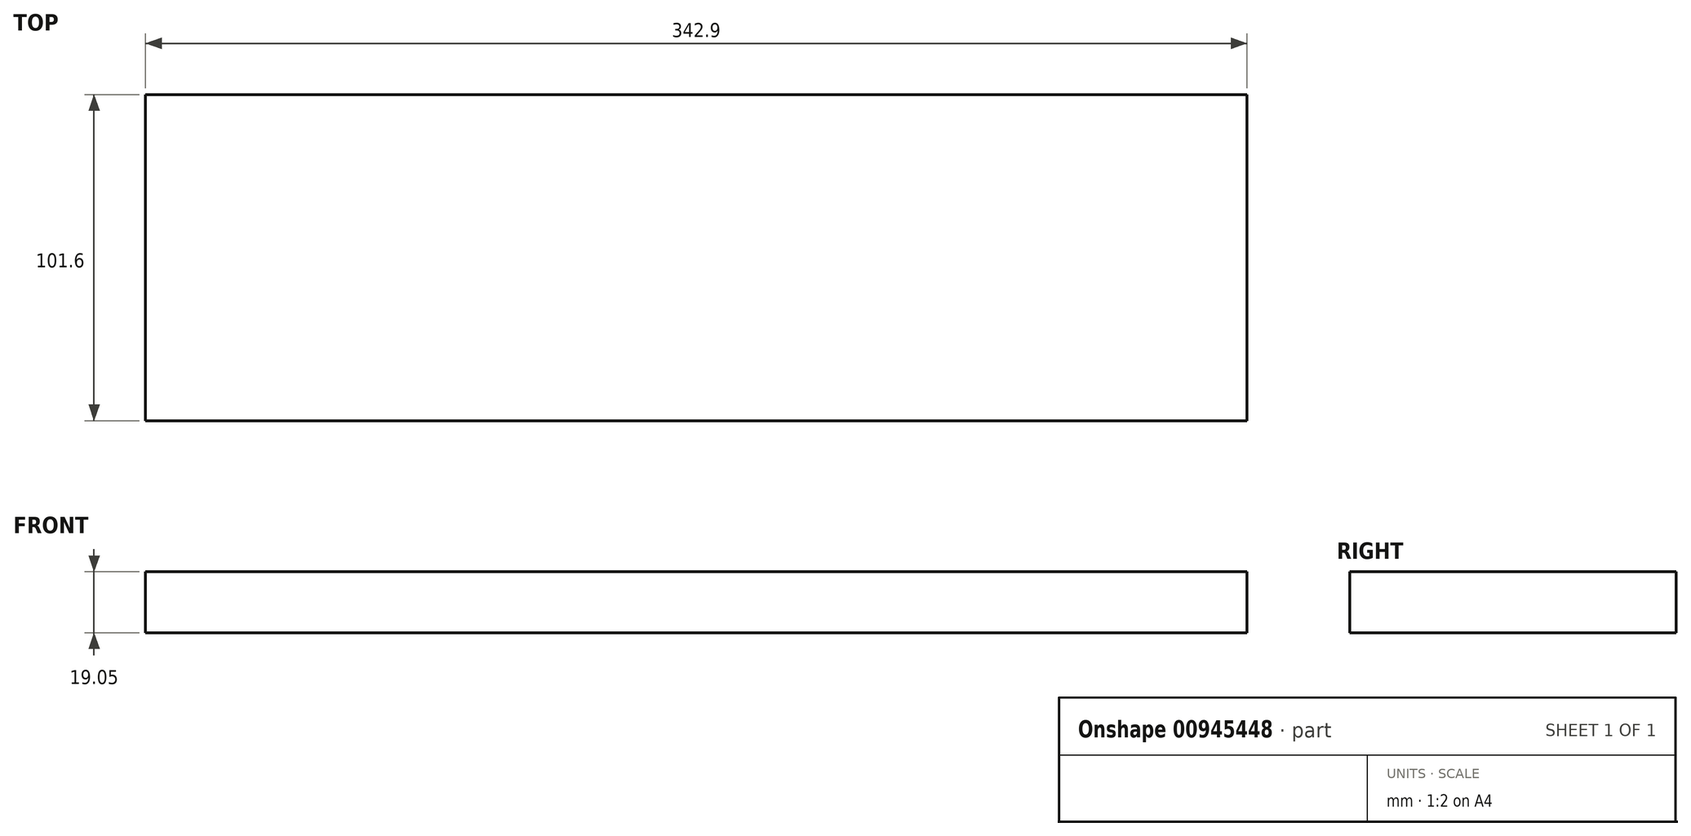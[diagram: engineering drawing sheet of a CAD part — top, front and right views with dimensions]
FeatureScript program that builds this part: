
annotation { "Feature Type Name" : "Feature", "Feature Type Description" : "" }
export const myFeature = defineFeature(function(context is Context, id is Id, definition is map)
    precondition{}
    {
        {
            var Q0;
            Q0=qCreatedBy(makeId("Top.planeOp"),FACE);
            var sketch = newSketch(context, id + "F0", { "sketchPlane" : qUnion([Q0])});
            skLineSegment(sketch, "E0.bottom", {"start": v(0, 0) * mm, "end": v(342.9, 0) * mm});
            skLineSegment(sketch, "E0.top", {"start": v(0, 101.6) * mm, "end": v(342.9, 101.6) * mm});
            skLineSegment(sketch, "E0.left", {"start": v(0, 0) * mm, "end": v(0, 101.6) * mm});
            skLineSegment(sketch, "E0.right", {"start": v(342.9, 0) * mm, "end": v(342.9, 101.6) * mm});
            skSolve(sketch);
        }
        {
            var Q0;
            Q0=makeQuery(id+"F0.imprint","IMPRINT",FACE,{"disambiguationData":[TD([[makeQuery(id+"F0.imprint","IMPRINT",EDGE,{"derivedFrom":sQuery(id+"F0.wireOp",EDGE,"E0.bottom")}),1.0]])]});
            extrude(context, id + "F1", {"entities" : qUnion([Q0]), "depth" : 19.05 * mm, "offsetDistance" : 25.4 * mm});
        }
    });
